# Revit family: Tap-IntervalTap-WithFilter-Vitra-A45225
name_source: partatom
category: Plumbing Fixtures
revit_build: Autodesk Revit 2017 (Build: 20160225_1515(x64)
units: mm (PartAtom-declared; Revit-internal decimal feet)

## family parameters
Cut with Voids When Loaded = No
Host = Face
OmniClass Number = 23.45.55.17
OmniClass Title = Mixing Faucets
Part Type = Normal
Room Calculation Point = No
Round Connector Dimension = Use Diameter
Shared = Yes

## types (1)
- Tap-IntervalTap-WithFilter-Vitra-A45225
    Article No. (default) = A45225
    BIMobject category = Sanitary - Taps & Mixers
    Brand = Artema
    CW Connection = Yes
    Coating Material = Chrome
    Color = Chrome
    Connection Diameter (mm) = 15 mm  [stored 0.0492126 ft]
    Default Elevation = 850 mm
    Description = Interval Tap - With Filter
    Design country = Turkey
    HW Connection = No
    Hot Water Supply (max.) = 80 °C
    Hot Water temperature, factory set to = 38 °C
    IFC Classification = Sanitary Terminal
    Main Material = Brass
    Manufacturer = VitrA
    Manufacturer name = Vitra
    Masterformat 2014 Code = 22 40 00
    Masterformat 2014 Description = Plumbing Fixtures
    Min. flow pressure of = 0.5 bar
    Model = A45225
    Mounting type = Wall Mounted - Pipe Connect
    NBS Referans Code = 31-06
    NBS Referans Description = Bathing Fittings
    Nominal Depth (mm) = 86 mm  [stored 0.282152 ft]
    Nominal Height (mm) = 100 mm  [stored 0.328084 ft]
    Nominal Width (mm) = 60 mm
    Number Of Connections = 1
    OmniClass Code = 23-27 31 29
    OmniClass Description = Mixing Valves
    Product SKU = A45225
    Product Type = Stop Valve
    Product certification = https://www.vitraglobal.com
    Product group = Stop Valve
    Product url = https://www.vitra.com.tr
    Range of Hot Water Supply = 5 - 65 °C
    Range of flow pressure = 1 - 5 bar
    Technical description = https://www.vitra.com.tr
    Test Pressure = 16 bar
    UNSPSC Code = 3018
    UNSPSC Description = Plumbing fixtures
    URL = https://vitraglobal.com
    Uniclass 1.4 Code = L725111
    Uniclass 1.4 Description = Taps
    Uniclass 2.0 Code = PR-31-06
    Uniclass 2.0 Description = Bathing Fittings
    Uniclass 2015 Code = Pr_40_20_87_09
    Uniclass 2015 Name = Bath taps
    Uniformat II Code = 22 40 00
    Uniformat II Description = Plumbing Fixture
    Vent Connection = No
    Warranty Period (Year) = 10 Years
    Waste Connection = No
    Weight Net (kg) = 0.5
    Youtube = https://www.youtube.com

note: [stored X ft] marks values corroborated as IEEE doubles in the binary element streams (Revit-internal decimal feet)

## geometry (parser evidence)
native form markers: Sweep x2
no freeform markers — native parametric forms only
